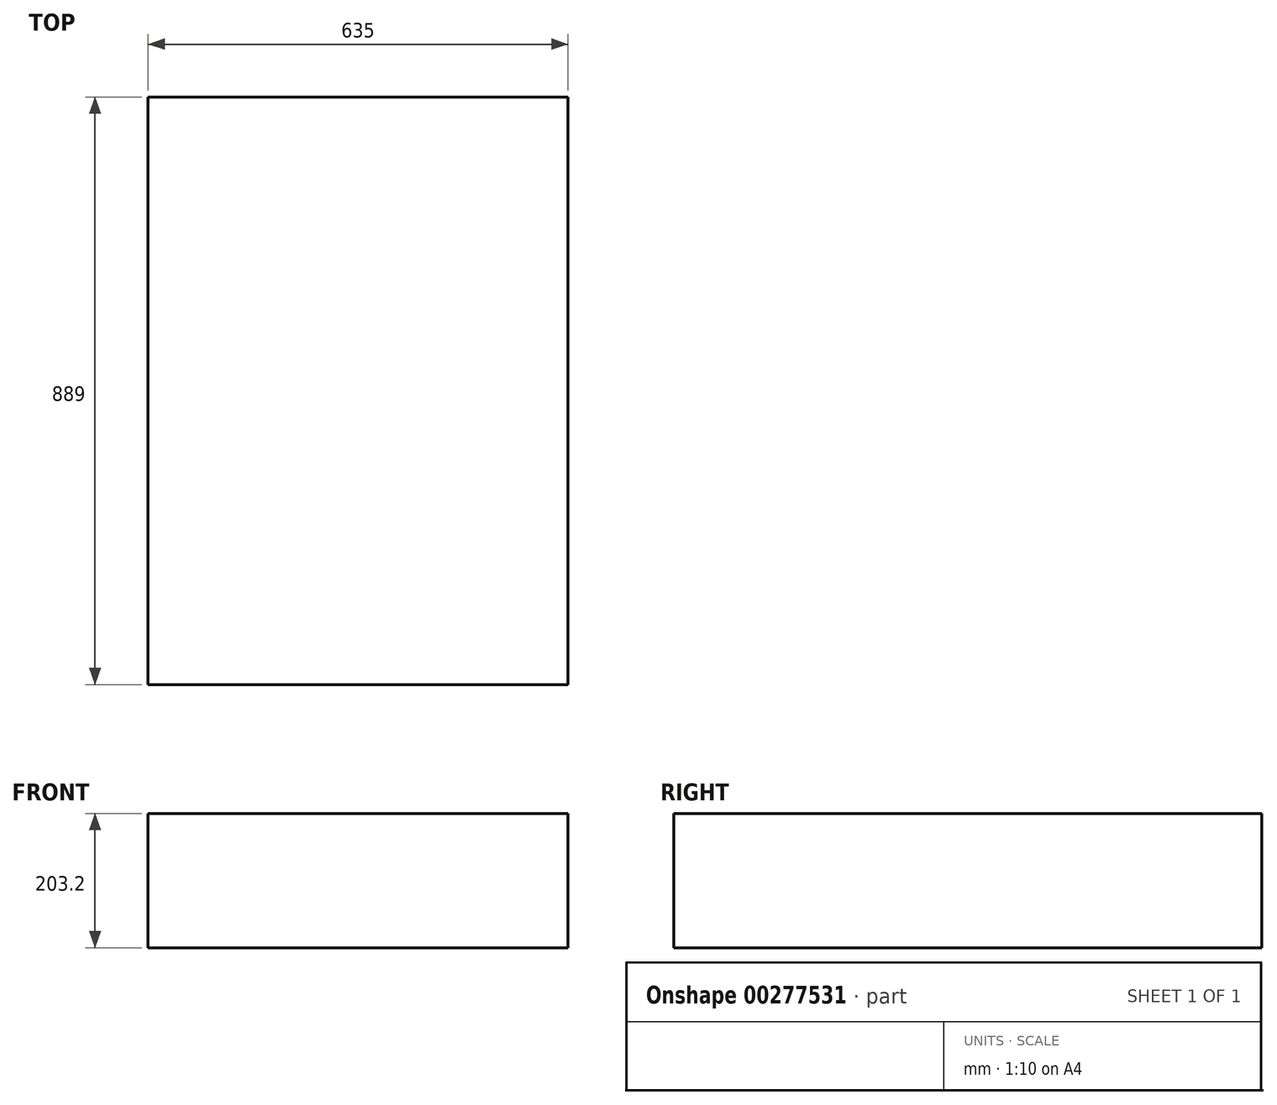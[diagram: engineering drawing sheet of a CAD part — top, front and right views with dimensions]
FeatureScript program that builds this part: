
annotation { "Feature Type Name" : "Feature", "Feature Type Description" : "" }
export const myFeature = defineFeature(function(context is Context, id is Id, definition is map)
    precondition{}
    {
        {
            var Q0;
            Q0=qCreatedBy(makeId("Top.planeOp"),FACE);
            var sketch = newSketch(context, id + "F0", { "sketchPlane" : qUnion([Q0])});
            skLineSegment(sketch, "E0.bottom", {"start": v(-325.04, -380.19) * mm, "end": v(309.96, -380.19) * mm});
            skLineSegment(sketch, "E0.top", {"start": v(-325.04, 508.81) * mm, "end": v(309.96, 508.81) * mm});
            skLineSegment(sketch, "E0.left", {"start": v(-325.04, -380.19) * mm, "end": v(-325.04, 508.81) * mm});
            skLineSegment(sketch, "E0.right", {"start": v(309.96, -380.19) * mm, "end": v(309.96, 508.81) * mm});
            skSolve(sketch);
        }
        {
            var Q0;
            Q0 = qSketchRegion(id + "F0", true);
            extrude(context, id + "F1", {"entities" : qUnion([Q0]), "depth" : 203.2 * mm});
        }
    });
